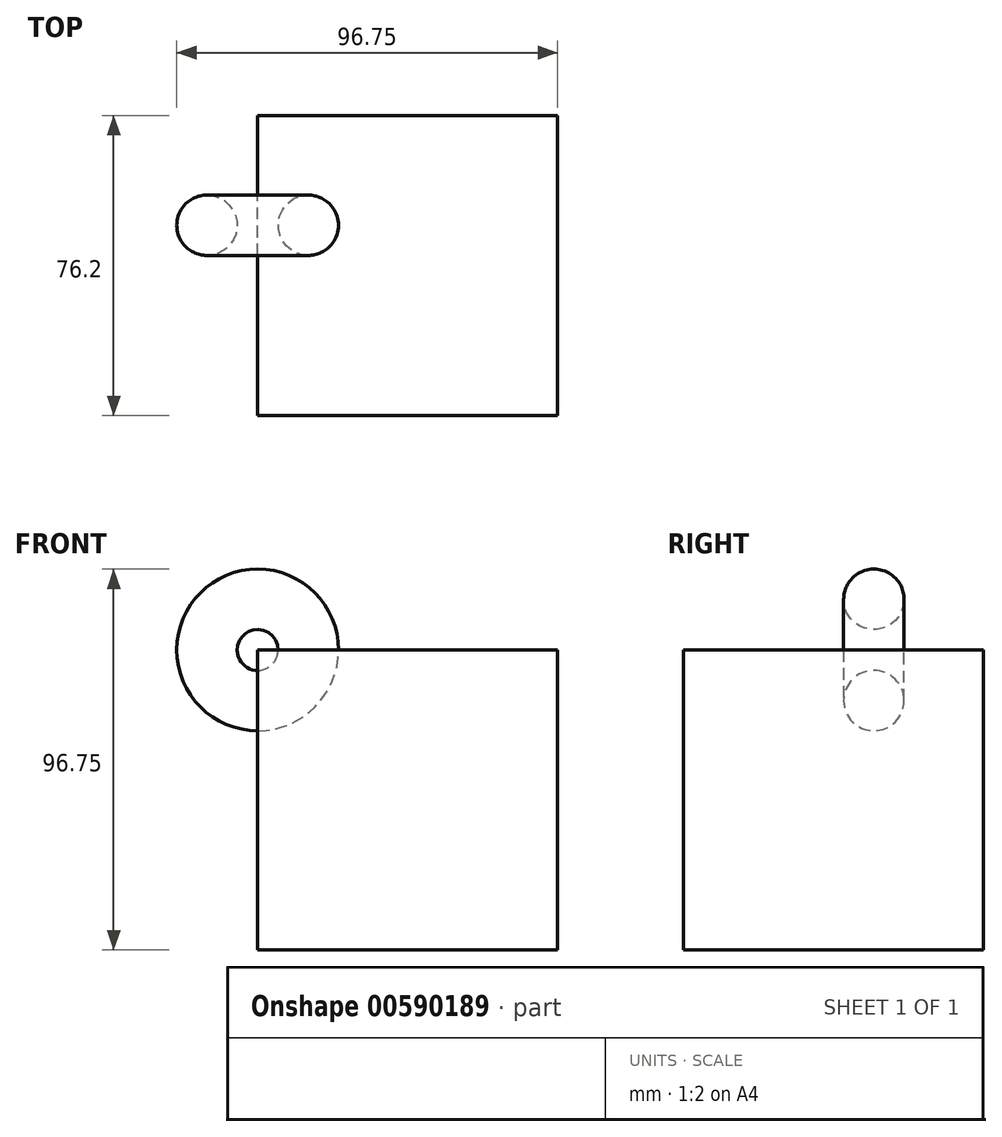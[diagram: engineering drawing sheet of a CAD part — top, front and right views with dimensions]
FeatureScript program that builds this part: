
annotation { "Feature Type Name" : "Feature", "Feature Type Description" : "" }
export const myFeature = defineFeature(function(context is Context, id is Id, definition is map)
    precondition{}
    {
        {
            var Q0;
            Q0=qCreatedBy(makeId("Front.planeOp"),FACE);
            var sketch = newSketch(context, id + "F0", { "sketchPlane" : qUnion([Q0])});
            skLineSegment(sketch, "E0", {"start": v(0, 0) * mm, "end": v(76.2, 0) * mm});
            skLineSegment(sketch, "E1", {"start": v(76.2, 0) * mm, "end": v(76.2, 76.2) * mm});
            skLineSegment(sketch, "E2", {"start": v(76.2, 76.2) * mm, "end": v(0, 76.2) * mm});
            skLineSegment(sketch, "E3", {"start": v(0, 76.2) * mm, "end": v(0, 0) * mm});
            skSolve(sketch);
        }
        {
            var Q0;
            Q0 = qSketchRegion(id + "F0", true);
            extrude(context, id + "F1", {"entities" : qUnion([Q0]), "depth" : 76.2 * mm, "offsetDistance" : 25.4 * mm});
        }
        {
            var Q0;
            Q0=makeQuery(id+"F1.opExtrude","CAP_FACE",FACE,{"disambiguationData":[OSD([sQuery(id+"F0.wireOp",EDGE,"E0"),sQuery(id+"F0.wireOp",EDGE,"E1"),sQuery(id+"F0.wireOp",EDGE,"E2"),sQuery(id+"F0.wireOp",EDGE,"E3")])],"isStart":false});
            var sketch = newSketch(context, id + "F2", { "sketchPlane" : qUnion([Q0])});
            skCircle(sketch, "E4", {"center": v(42.1, 13.02) * mm, "radius": 7.67 * mm});
            skSolve(sketch);
        }
        {
            var Q0;
            Q0=sQuery(id+"F2.wireOp",EDGE,"E4");
            var Q1;
            Q1=makeQuery(id+"F1.opExtrude","CAP_EDGE",EDGE,{"disambiguationData":[OSD([sQuery(id+"F0.wireOp",EDGE,"E0")])],"isStart":false});
            revolve(context, id + "F3", {"bodyType" : ToolBodyType.SURFACE, "surfaceEntities" : qUnion([Q0]), "axis" : qUnion([Q1]), "revolveType" : RevolveType.FULL});
        }
        {
            var Q0;
            Q0=makeQuery(id+"F1.opExtrude","SWEPT_FACE",FACE,{"disambiguationData":[OSD([sQuery(id+"F0.wireOp",EDGE,"E3")])]});
            var sketch = newSketch(context, id + "F4", { "sketchPlane" : qUnion([Q0])});
            skSolve(sketch);
        }
        {
            var Q0;
            {var subQ0=sQuery(id+"F0.wireOp",EDGE,"E3");Q0=makeQuery(id+"F4.imprint","IMPRINT",FACE,{"disambiguationData":[TD([[makeQuery(id+"F4.imprint","IMPRINT",EDGE,{"derivedFrom":makeQuery(id+"F1.opExtrude","CAP_EDGE",EDGE,{"disambiguationData":[OSD([subQ0])],"isStart":true})}),1.0]])]});}
            var sketch = newSketch(context, id + "F5", { "sketchPlane" : qUnion([Q0])});
            skCircle(sketch, "E5", {"center": v(27.85, 63.32) * mm, "radius": 7.67 * mm});
            skSolve(sketch);
        }
        {
            var Q0;
            Q0=makeQuery(id+"F5.imprint","IMPRINT",FACE,{"disambiguationData":[TD([[makeQuery(id+"F5.imprint","IMPRINT",EDGE,{"derivedFrom":sQuery(id+"F5.wireOp",EDGE,"E5")}),1.0]])]});
            var Q1;
            Q1=makeQuery(id+"F1.opExtrude","SWEPT_EDGE",EDGE,{"disambiguationData":[OSD([sQuery(id+"F0.wireOp",EDGE,"E2"),sQuery(id+"F0.wireOp",EDGE,"E3")])]});
            revolve(context, id + "F6", {"entities" : qUnion([Q0]), "axis" : qUnion([Q1]), "revolveType" : RevolveType.FULL});
        }
    });
